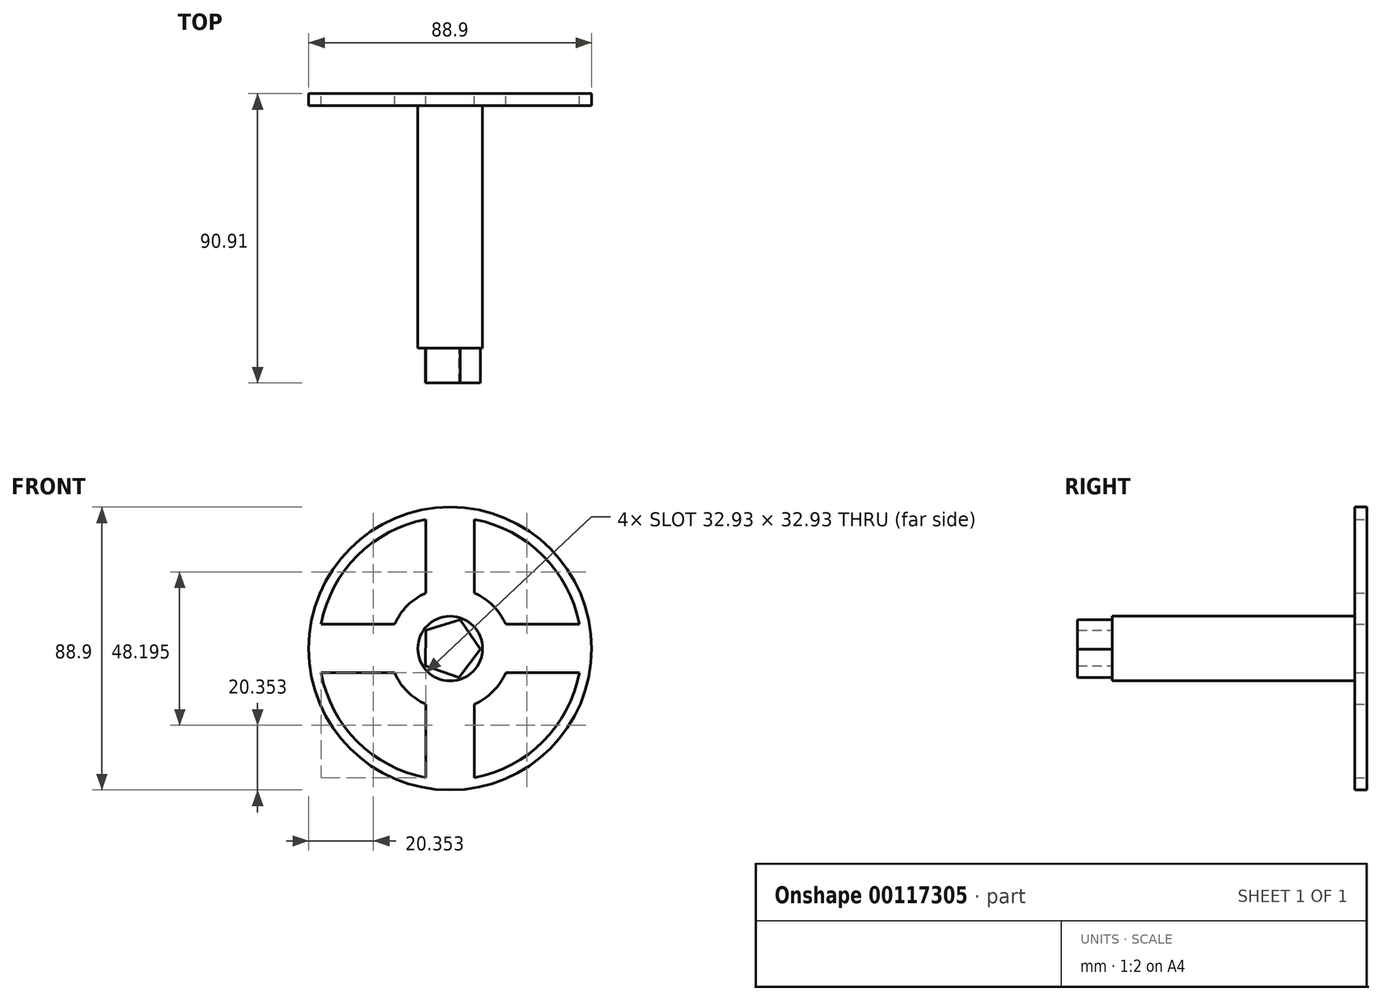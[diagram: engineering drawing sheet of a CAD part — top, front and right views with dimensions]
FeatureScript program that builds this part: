
annotation { "Feature Type Name" : "Feature", "Feature Type Description" : "" }
export const myFeature = defineFeature(function(context is Context, id is Id, definition is map)
    precondition{}
    {
        {
            var Q0;
            Q0=qCreatedBy(makeId("Front.planeOp"),FACE);
            var sketch = newSketch(context, id + "F0", { "sketchPlane" : qUnion([Q0])});
            skCircle(sketch, "E0", {"center": v(0, 0) * mm, "radius": 44.45 * mm});
            skCircle(sketch, "E1", {"center": v(0, 0) * mm, "radius": 19.05 * mm});
            skCircle(sketch, "E2", {"center": v(0, 0) * mm, "radius": 41.28 * mm});
            skLineSegment(sketch, "E3.bottom", {"start": v(-40.56, 7.63) * mm, "end": v(-17.45, 7.63) * mm});
            skLineSegment(sketch, "E3.top", {"start": v(-40.56, -7.63) * mm, "end": v(-17.45, -7.63) * mm});
            skLineSegment(sketch, "E3.left", {"start": v(-40.56, 7.63) * mm, "end": v(-40.56, -7.63) * mm});
            skLineSegment(sketch, "E3.right", {"start": v(-17.45, 7.63) * mm, "end": v(-17.45, -7.63) * mm});
            skPoint(sketch, "E3.middle", {"position": v(-29, 0) * mm});
            skLineSegment(sketch, "E4.1.0", {"start": v(-7.63, -40.56) * mm, "end": v(-7.63, -17.45) * mm});
            skLineSegment(sketch, "E4.1.1", {"start": v(-7.63, -40.56) * mm, "end": v(7.63, -40.56) * mm});
            skLineSegment(sketch, "E4.1.2", {"start": v(7.63, -40.56) * mm, "end": v(7.63, -17.45) * mm});
            skLineSegment(sketch, "E4.1.3", {"start": v(-7.63, -17.45) * mm, "end": v(7.63, -17.45) * mm});
            skLineSegment(sketch, "E4.2.0", {"start": v(40.56, -7.63) * mm, "end": v(17.45, -7.63) * mm});
            skLineSegment(sketch, "E4.2.1", {"start": v(40.56, -7.63) * mm, "end": v(40.56, 7.63) * mm});
            skLineSegment(sketch, "E4.2.2", {"start": v(40.56, 7.63) * mm, "end": v(17.45, 7.63) * mm});
            skLineSegment(sketch, "E4.2.3", {"start": v(17.45, -7.63) * mm, "end": v(17.45, 7.63) * mm});
            skLineSegment(sketch, "E4.3.0", {"start": v(7.63, 40.56) * mm, "end": v(7.63, 17.45) * mm});
            skLineSegment(sketch, "E4.3.1", {"start": v(7.63, 40.56) * mm, "end": v(-7.63, 40.56) * mm});
            skLineSegment(sketch, "E4.3.2", {"start": v(-7.63, 40.56) * mm, "end": v(-7.63, 17.45) * mm});
            skLineSegment(sketch, "E4.3.3", {"start": v(7.63, 17.45) * mm, "end": v(-7.63, 17.45) * mm});
            skSolve(sketch);
        }
        {
            var Q0;
            Q0 = qSketchRegion(id + "F0", true);
            var Q1;
            {var subQ1=sQuery(id+"F0.wireOp",EDGE,"E3.bottom");Q1=makeQuery(id+"F0.imprint","IMPRINT",FACE,{"disambiguationData":[TD([[makeQuery(id+"F0.imprint","IMPRINT",EDGE,{"derivedFrom":subQ1}),-1.0]])]});}
            var Q2;
            {var subQ3=sQuery(id+"F0.wireOp",EDGE,"E3.right");Q2=makeQuery(id+"F0.imprint","IMPRINT",FACE,{"disambiguationData":[TD([[makeQuery(id+"F0.imprint","IMPRINT",EDGE,{"derivedFrom":subQ3}),1.0]])]});}
            var Q3;
            {var subQ0=sQuery(id+"F0.wireOp",EDGE,"E3.right");Q3=makeQuery(id+"F0.imprint","IMPRINT",FACE,{"disambiguationData":[TD([[makeQuery(id+"F0.imprint","IMPRINT",EDGE,{"derivedFrom":subQ0}),-1.0]])]});}
            var Q4;
            {var subQ0=sQuery(id+"F0.wireOp",EDGE,"E4.3.3");Q4=makeQuery(id+"F0.imprint","IMPRINT",FACE,{"disambiguationData":[TD([[makeQuery(id+"F0.imprint","IMPRINT",EDGE,{"derivedFrom":subQ0}),-1.0]])]});}
            var Q5;
            {var subQ0=sQuery(id+"F0.wireOp",EDGE,"E4.2.3");Q5=makeQuery(id+"F0.imprint","IMPRINT",FACE,{"disambiguationData":[TD([[makeQuery(id+"F0.imprint","IMPRINT",EDGE,{"derivedFrom":subQ0}),-1.0]])]});}
            var Q6;
            {var subQ0=sQuery(id+"F0.wireOp",EDGE,"E4.2.1");Q6=makeQuery(id+"F0.imprint","IMPRINT",FACE,{"disambiguationData":[TD([[makeQuery(id+"F0.imprint","IMPRINT",EDGE,{"derivedFrom":subQ0}),-1.0]])]});}
            var Q7;
            {var subQ1=sQuery(id+"F0.wireOp",EDGE,"E4.2.0");Q7=makeQuery(id+"F0.imprint","IMPRINT",FACE,{"disambiguationData":[TD([[makeQuery(id+"F0.imprint","IMPRINT",EDGE,{"derivedFrom":subQ1}),-1.0]])]});}
            var Q8;
            {var subQ1=sQuery(id+"F0.wireOp",EDGE,"E4.1.0");Q8=makeQuery(id+"F0.imprint","IMPRINT",FACE,{"disambiguationData":[TD([[makeQuery(id+"F0.imprint","IMPRINT",EDGE,{"derivedFrom":subQ1}),-1.0]])]});}
            var Q9;
            {var subQ0=sQuery(id+"F0.wireOp",EDGE,"E4.1.3");Q9=makeQuery(id+"F0.imprint","IMPRINT",FACE,{"disambiguationData":[TD([[makeQuery(id+"F0.imprint","IMPRINT",EDGE,{"derivedFrom":subQ0}),-1.0]])]});}
            var Q10;
            {var subQ0=sQuery(id+"F0.wireOp",EDGE,"E4.1.1");Q10=makeQuery(id+"F0.imprint","IMPRINT",FACE,{"disambiguationData":[TD([[makeQuery(id+"F0.imprint","IMPRINT",EDGE,{"derivedFrom":subQ0}),-1.0]])]});}
            var Q11;
            {var subQ0=sQuery(id+"F0.wireOp",EDGE,"E3.left");Q11=makeQuery(id+"F0.imprint","IMPRINT",FACE,{"disambiguationData":[TD([[makeQuery(id+"F0.imprint","IMPRINT",EDGE,{"derivedFrom":subQ0}),-1.0]])]});}
            var Q12;
            {var subQ1=sQuery(id+"F0.wireOp",EDGE,"E4.3.0");Q12=makeQuery(id+"F0.imprint","IMPRINT",FACE,{"disambiguationData":[TD([[makeQuery(id+"F0.imprint","IMPRINT",EDGE,{"derivedFrom":subQ1}),-1.0]])]});}
            var Q13;
            {var subQ0=sQuery(id+"F0.wireOp",EDGE,"E4.3.1");Q13=makeQuery(id+"F0.imprint","IMPRINT",FACE,{"disambiguationData":[TD([[makeQuery(id+"F0.imprint","IMPRINT",EDGE,{"derivedFrom":subQ0}),-1.0]])]});}
            extrude(context, id + "F1", {"entities" : qUnion([Q0, Q1, Q2, Q3, Q4, Q5, Q6, Q7, Q8, Q9, Q10, Q11, Q12, Q13]), "depth" : 3.8 * mm});
        }
        {
            var Q0;
            Q0=makeQuery(id+"F1.opExtrude","CAP_FACE",FACE,{"disambiguationData":[OSD([sQuery(id+"F0.wireOp",EDGE,"E0"),sQuery(id+"F0.wireOp",EDGE,"E1"),sQuery(id+"F0.wireOp",EDGE,"E2"),sQuery(id+"F0.wireOp",EDGE,"E3.bottom"),sQuery(id+"F0.wireOp",EDGE,"E3.top"),sQuery(id+"F0.wireOp",EDGE,"E4.1.0"),sQuery(id+"F0.wireOp",EDGE,"E4.1.2"),sQuery(id+"F0.wireOp",EDGE,"E4.2.0"),sQuery(id+"F0.wireOp",EDGE,"E4.2.2"),sQuery(id+"F0.wireOp",EDGE,"E4.3.0"),sQuery(id+"F0.wireOp",EDGE,"E4.3.2")])],"isStart":false});
            var sketch = newSketch(context, id + "F2", { "sketchPlane" : qUnion([Q0])});
            skCircle(sketch, "E5", {"center": v(0, 0) * mm, "radius": 10.16 * mm});
            skSolve(sketch);
        }
        {
            var Q0;
            Q0 = qSketchRegion(id + "F2", true);
            extrude(context, id + "F3", {"entities" : qUnion([Q0]), "operationType" : NewBodyOperationType.ADD, "depth" : 76.2 * mm});
        }
        {
            var Q0;
            Q0=makeQuery(id+"F3.opExtrude","CAP_FACE",FACE,{"disambiguationData":[OSD([sQuery(id+"F2.wireOp",EDGE,"E5")])],"isStart":false});
            var sketch = newSketch(context, id + "F4", { "sketchPlane" : qUnion([Q0])});
            skCircle(sketch, "E6.cCircle", {"center": v(0, 0) * mm, "radius": 9.53 * mm, "construction": true});
            skLineSegment(sketch, "E6.0", {"start": v(-7.6, 5.73) * mm, "end": v(3.1, 9) * mm});
            skLineSegment(sketch, "E6.1", {"start": v(3.1, 9) * mm, "end": v(9.52, -0.17) * mm});
            skLineSegment(sketch, "E6.2", {"start": v(9.52, -0.17) * mm, "end": v(2.78, -9.1) * mm});
            skLineSegment(sketch, "E6.3", {"start": v(2.78, -9.1) * mm, "end": v(-7.8, -5.46) * mm});
            skLineSegment(sketch, "E6.4", {"start": v(-7.8, -5.46) * mm, "end": v(-7.6, 5.73) * mm});
            skSolve(sketch);
        }
        {
            var Q0;
            Q0 = qSketchRegion(id + "F4", true);
            extrude(context, id + "F5", {"entities" : qUnion([Q0]), "operationType" : NewBodyOperationType.ADD, "depth" : 10.9 * mm});
        }
    });
